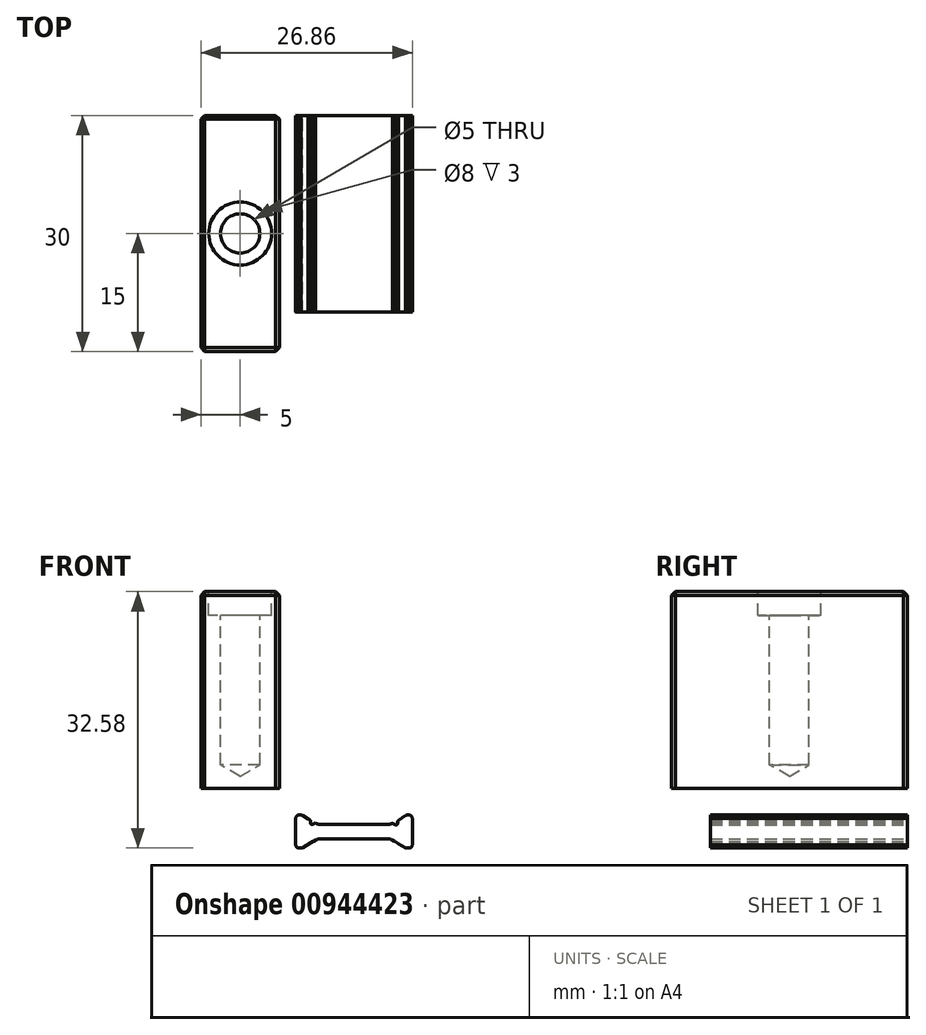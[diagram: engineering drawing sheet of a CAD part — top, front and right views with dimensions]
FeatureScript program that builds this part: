
annotation { "Feature Type Name" : "Feature", "Feature Type Description" : "" }
export const myFeature = defineFeature(function(context is Context, id is Id, definition is map)
    precondition{}
    {
        {
            var Q0;
            Q0=qCreatedBy(makeId("Front.planeOp"),FACE);
            var sketch = newSketch(context, id + "F0", { "sketchPlane" : qUnion([Q0])});
            skArc(sketch, "E0", {"start": v(-30.4, -3.2) * mm, "mid": v(-30.25, -3.55) * mm, "end": v(-29.9, -3.7) * mm});
            skLineSegment(sketch, "E1", {"start": v(-29.9, -3.7) * mm, "end": v(-29.4, -3.7) * mm});
            skArc(sketch, "E2", {"start": v(-29.4, -3.7) * mm, "mid": v(-29.19, -3.61) * mm, "end": v(-29.1, -3.4) * mm});
            skLineSegment(sketch, "E3", {"start": v(-29.1, -3.4) * mm, "end": v(-29.1, -1.7) * mm});
            skLineSegment(sketch, "E4", {"start": v(-29.1, -1.7) * mm, "end": v(-4.3, -1.7) * mm});
            skLineSegment(sketch, "E5", {"start": v(-4.3, -1.7) * mm, "end": v(-4.3, -16.5) * mm});
            skLineSegment(sketch, "E6", {"start": v(-4.3, -16.5) * mm, "end": v(-38.5, -16.5) * mm});
            skLineSegment(sketch, "E7", {"start": v(-38.5, -16.5) * mm, "end": v(-38.5, -7.78) * mm});
            skArc(sketch, "E8", {"start": v(-38.5, -7.78) * mm, "mid": v(-38.1, -6.14) * mm, "end": v(-36.97, -4.89) * mm});
            skArc(sketch, "E9", {"start": v(-36.97, -4.89) * mm, "mid": v(-33.82, -3.17) * mm, "end": v(-30.4, -2.1) * mm});
            skLineSegment(sketch, "E10", {"start": v(-30.4, -2.1) * mm, "end": v(-30.4, -3.2) * mm});
            skArc(sketch, "E11", {"start": v(-2.7, -12.19) * mm, "mid": v(-2.62, -12) * mm, "end": v(-2.43, -11.92) * mm});
            skLineSegment(sketch, "E12", {"start": v(-2.43, -11.92) * mm, "end": v(-2.15, -11.92) * mm});
            skArc(sketch, "E13", {"start": v(-2.15, -11.92) * mm, "mid": v(-2.1, -11.93) * mm, "end": v(-2.05, -11.95) * mm});
            skLineSegment(sketch, "E14", {"start": v(-2.05, -11.95) * mm, "end": v(-0.5, -12.89) * mm});
            skArc(sketch, "E15", {"start": v(-0.5, -12.89) * mm, "mid": v(-0.3, -12.9) * mm, "end": v(-0.2, -12.72) * mm});
            skLineSegment(sketch, "E16", {"start": v(-0.2, -12.72) * mm, "end": v(-0.2, -11.3) * mm});
            skArc(sketch, "E17", {"start": v(-0.2, -11.3) * mm, "mid": v(-0.33, -10.8) * mm, "end": v(-0.68, -10.44) * mm});
            skLineSegment(sketch, "E18", {"start": v(-0.68, -10.44) * mm, "end": v(-2.5, -9.33) * mm});
            skArc(sketch, "E19", {"start": v(-2.5, -9.33) * mm, "mid": v(-2.57, -9.26) * mm, "end": v(-2.6, -9.16) * mm});
            skArc(sketch, "E20", {"start": v(-2.6, -9.16) * mm, "mid": v(-2.57, -9.06) * mm, "end": v(-2.5, -8.99) * mm});
            skLineSegment(sketch, "E21", {"start": v(-2.5, -8.99) * mm, "end": v(-0.68, -7.87) * mm});
            skArc(sketch, "E22", {"start": v(-0.68, -7.87) * mm, "mid": v(-0.33, -7.5) * mm, "end": v(-0.2, -7.02) * mm});
            skLineSegment(sketch, "E23", {"start": v(-0.2, -7.02) * mm, "end": v(-0.2, -5.6) * mm});
            skArc(sketch, "E24", {"start": v(-0.2, -5.6) * mm, "mid": v(-0.3, -5.42) * mm, "end": v(-0.5, -5.43) * mm});
            skLineSegment(sketch, "E25", {"start": v(-0.5, -5.43) * mm, "end": v(-2.05, -6.37) * mm});
            skArc(sketch, "E26", {"start": v(-2.05, -6.37) * mm, "mid": v(-2.1, -6.4) * mm, "end": v(-2.15, -6.4) * mm});
            skLineSegment(sketch, "E27", {"start": v(-2.15, -6.4) * mm, "end": v(-2.43, -6.4) * mm});
            skArc(sketch, "E28", {"start": v(-2.43, -6.4) * mm, "mid": v(-2.62, -6.32) * mm, "end": v(-2.7, -6.13) * mm});
            skLineSegment(sketch, "E29", {"start": v(-2.7, -6.13) * mm, "end": v(-2.7, -2.05) * mm});
            skArc(sketch, "E30", {"start": v(-2.7, -2.05) * mm, "mid": v(-2.7, -2.03) * mm, "end": v(-2.69, -2.01) * mm});
            skArc(sketch, "E31", {"start": v(-2.69, -2.01) * mm, "mid": v(-2.51, -1.78) * mm, "end": v(-2.22, -1.8) * mm});
            skLineSegment(sketch, "E32", {"start": v(-2.22, -1.8) * mm, "end": v(-0.9, -2.7) * mm});
            skArc(sketch, "E33", {"start": v(-0.9, -2.7) * mm, "mid": v(-0.84, -2.78) * mm, "end": v(-0.82, -2.88) * mm});
            skLineSegment(sketch, "E34", {"start": v(-0.82, -2.88) * mm, "end": v(-0.83, -3.05) * mm});
            skArc(sketch, "E35", {"start": v(-0.83, -3.05) * mm, "mid": v(-0.75, -3.23) * mm, "end": v(-0.55, -3.25) * mm});
            skLineSegment(sketch, "E36", {"start": v(-0.55, -3.25) * mm, "end": v(-0.1, -3.03) * mm});
            skArc(sketch, "E37", {"start": v(-0.1, -3.03) * mm, "mid": v(-0.05, -3) * mm, "end": v(-0.01, -2.96) * mm});
            skLineSegment(sketch, "E38", {"start": v(-0.01, -2.96) * mm, "end": v(1.44, -0.66) * mm});
            skArc(sketch, "E39", {"start": v(1.44, -0.66) * mm, "mid": v(1.44, -0.36) * mm, "end": v(1.18, -0.2) * mm});
            skLineSegment(sketch, "E40", {"start": v(1.18, -0.2) * mm, "end": v(-2.75, -0.2) * mm});
            skLineSegment(sketch, "E41", {"start": v(-2.75, -0.2) * mm, "end": v(-16, -0.2) * mm});
            skArc(sketch, "E42", {"start": v(-16, -0.2) * mm, "mid": v(-16.36, -0.05) * mm, "end": v(-16.5, 0.3) * mm});
            skLineSegment(sketch, "E43", {"start": v(-16.5, 0.3) * mm, "end": v(-16.5, 21.41) * mm});
            skArc(sketch, "E44", {"start": v(-16.5, 21.41) * mm, "mid": v(-16.4, 21.64) * mm, "end": v(-16.17, 21.71) * mm});
            skLineSegment(sketch, "E45", {"start": v(-16.17, 21.71) * mm, "end": v(-15.26, 21.6) * mm});
            skArc(sketch, "E46", {"start": v(-15.26, 21.6) * mm, "mid": v(-15.05, 21.69) * mm, "end": v(-14.96, 21.9) * mm});
            skLineSegment(sketch, "E47", {"start": v(-14.96, 21.9) * mm, "end": v(-14.96, 23.3) * mm});
            skArc(sketch, "E48", {"start": v(-14.96, 23.3) * mm, "mid": v(-15.02, 23.48) * mm, "end": v(-15.18, 23.58) * mm});
            skLineSegment(sketch, "E49", {"start": v(-15.18, 23.58) * mm, "end": v(-22.2, 25.46) * mm});
            skArc(sketch, "E50", {"start": v(-22.2, 25.46) * mm, "mid": v(-22.46, 25.5) * mm, "end": v(-22.72, 25.46) * mm});
            skLineSegment(sketch, "E51", {"start": v(-22.72, 25.46) * mm, "end": v(-29.73, 23.58) * mm});
            skArc(sketch, "E52", {"start": v(-29.73, 23.58) * mm, "mid": v(-29.9, 23.48) * mm, "end": v(-29.96, 23.3) * mm});
            skLineSegment(sketch, "E53", {"start": v(-29.96, 23.3) * mm, "end": v(-29.96, 14.56) * mm});
            skArc(sketch, "E54", {"start": v(-29.96, 14.56) * mm, "mid": v(-29.49, 13.28) * mm, "end": v(-28.3, 12.6) * mm});
            skLineSegment(sketch, "E55", {"start": v(-28.3, 12.6) * mm, "end": v(-27.31, 12.42) * mm});
            skArc(sketch, "E56", {"start": v(-27.31, 12.42) * mm, "mid": v(-27.07, 12.48) * mm, "end": v(-26.96, 12.71) * mm});
            skLineSegment(sketch, "E57", {"start": v(-26.96, 12.71) * mm, "end": v(-26.96, 13.52) * mm});
            skArc(sketch, "E58", {"start": v(-26.96, 13.52) * mm, "mid": v(-27.03, 13.72) * mm, "end": v(-27.2, 13.82) * mm});
            skLineSegment(sketch, "E59", {"start": v(-27.2, 13.82) * mm, "end": v(-28.3, 14.01) * mm});
            skArc(sketch, "E60", {"start": v(-28.3, 14.01) * mm, "mid": v(-28.49, 14.12) * mm, "end": v(-28.56, 14.3) * mm});
            skLineSegment(sketch, "E61", {"start": v(-28.56, 14.3) * mm, "end": v(-28.56, 22.01) * mm});
            skArc(sketch, "E62", {"start": v(-28.56, 22.01) * mm, "mid": v(-28.5, 22.2) * mm, "end": v(-28.33, 22.3) * mm});
            skLineSegment(sketch, "E63", {"start": v(-28.33, 22.3) * mm, "end": v(-24.76, 23.26) * mm});
            skArc(sketch, "E64", {"start": v(-24.76, 23.26) * mm, "mid": v(-24.7, 23.27) * mm, "end": v(-24.64, 23.28) * mm});
            skArc(sketch, "E65", {"start": v(-24.64, 23.28) * mm, "mid": v(-22.46, 23.3) * mm, "end": v(-20.27, 23.28) * mm});
            skArc(sketch, "E66", {"start": v(-20.27, 23.28) * mm, "mid": v(-20.21, 23.27) * mm, "end": v(-20.15, 23.26) * mm});
            skLineSegment(sketch, "E67", {"start": v(-20.15, 23.26) * mm, "end": v(-18.33, 22.77) * mm});
            skArc(sketch, "E68", {"start": v(-18.33, 22.77) * mm, "mid": v(-18.17, 22.66) * mm, "end": v(-18.1, 22.48) * mm});
            skLineSegment(sketch, "E69", {"start": v(-18.1, 22.48) * mm, "end": v(-18.1, 1.4) * mm});
            skArc(sketch, "E70", {"start": v(-18.1, 1.4) * mm, "mid": v(-18.2, 1.19) * mm, "end": v(-18.4, 1.1) * mm});
            skLineSegment(sketch, "E71", {"start": v(-18.4, 1.1) * mm, "end": v(-18.8, 1.1) * mm});
            skArc(sketch, "E72", {"start": v(-18.8, 1.1) * mm, "mid": v(-19.02, 1.01) * mm, "end": v(-19.1, 0.8) * mm});
            skArc(sketch, "E73", {"start": v(-19.1, 0.8) * mm, "mid": v(-19.4, 0.1) * mm, "end": v(-20.1, -0.2) * mm});
            skLineSegment(sketch, "E74", {"start": v(-20.1, -0.2) * mm, "end": v(-26.58, -0.2) * mm});
            skArc(sketch, "E75", {"start": v(-26.58, -0.2) * mm, "mid": v(-32.45, -1.08) * mm, "end": v(-37.8, -3.64) * mm});
            skArc(sketch, "E76", {"start": v(-37.8, -3.64) * mm, "mid": v(-39.42, -5.44) * mm, "end": v(-40, -7.78) * mm});
            skLineSegment(sketch, "E77", {"start": v(-40, -7.78) * mm, "end": v(-40, -25.2) * mm});
            skArc(sketch, "E78", {"start": v(-40, -25.2) * mm, "mid": v(-39.91, -25.41) * mm, "end": v(-39.7, -25.5) * mm});
            skLineSegment(sketch, "E79", {"start": v(-39.7, -25.5) * mm, "end": v(-37.42, -25.5) * mm});
            skArc(sketch, "E80", {"start": v(-37.42, -25.5) * mm, "mid": v(-37.17, -25.43) * mm, "end": v(-37, -25.25) * mm});
            skLineSegment(sketch, "E81", {"start": v(-37, -25.25) * mm, "end": v(-36.82, -24.95) * mm});
            skArc(sketch, "E82", {"start": v(-36.82, -24.95) * mm, "mid": v(-36.82, -24.45) * mm, "end": v(-37.25, -24.2) * mm});
            skLineSegment(sketch, "E83", {"start": v(-37.25, -24.2) * mm, "end": v(-38.6, -24.2) * mm});
            skLineSegment(sketch, "E84", {"start": v(-38.6, -24.2) * mm, "end": v(-38.6, -18) * mm});
            skLineSegment(sketch, "E85", {"start": v(-38.6, -18) * mm, "end": v(-4.5, -18) * mm});
            skArc(sketch, "E86", {"start": v(-4.5, -18) * mm, "mid": v(-4.29, -18.09) * mm, "end": v(-4.2, -18.3) * mm});
            skLineSegment(sketch, "E87", {"start": v(-4.2, -18.3) * mm, "end": v(-4.2, -24.1) * mm});
            skLineSegment(sketch, "E88", {"start": v(-4.2, -24.1) * mm, "end": v(-10.4, -24.1) * mm});
            skArc(sketch, "E89", {"start": v(-10.4, -24.1) * mm, "mid": v(-10.75, -24.24) * mm, "end": v(-10.9, -24.6) * mm});
            skLineSegment(sketch, "E90", {"start": v(-10.9, -24.6) * mm, "end": v(-10.9, -24.9) * mm});
            skArc(sketch, "E91", {"start": v(-10.9, -24.9) * mm, "mid": v(-10.75, -25.25) * mm, "end": v(-10.4, -25.4) * mm});
            skLineSegment(sketch, "E92", {"start": v(-10.4, -25.4) * mm, "end": v(-7.85, -25.4) * mm});
            skLineSegment(sketch, "E93", {"start": v(-7.85, -25.4) * mm, "end": v(-7.55, -25.1) * mm});
            skLineSegment(sketch, "E94", {"start": v(-7.55, -25.1) * mm, "end": v(-7.25, -25.4) * mm});
            skLineSegment(sketch, "E95", {"start": v(-7.25, -25.4) * mm, "end": v(-3.2, -25.4) * mm});
            skArc(sketch, "E96", {"start": v(-3.2, -25.4) * mm, "mid": v(-2.99, -25.31) * mm, "end": v(-2.9, -25.1) * mm});
            skLineSegment(sketch, "E97", {"start": v(-2.9, -25.1) * mm, "end": v(-2.9, -18.3) * mm});
            skArc(sketch, "E98", {"start": v(-2.9, -18.3) * mm, "mid": v(-2.81, -18.09) * mm, "end": v(-2.6, -18) * mm});
            skLineSegment(sketch, "E99", {"start": v(-2.6, -18) * mm, "end": v(1.17, -18) * mm});
            skArc(sketch, "E100", {"start": v(1.17, -18) * mm, "mid": v(1.44, -17.84) * mm, "end": v(1.43, -17.54) * mm});
            skLineSegment(sketch, "E101", {"start": v(1.43, -17.54) * mm, "end": v(-0.02, -15.24) * mm});
            skArc(sketch, "E102", {"start": v(-0.02, -15.24) * mm, "mid": v(-0.06, -15.2) * mm, "end": v(-0.1, -15.17) * mm});
            skLineSegment(sketch, "E103", {"start": v(-0.1, -15.17) * mm, "end": v(-0.55, -14.95) * mm});
            skArc(sketch, "E104", {"start": v(-0.55, -14.95) * mm, "mid": v(-0.75, -14.96) * mm, "end": v(-0.84, -15.14) * mm});
            skLineSegment(sketch, "E105", {"start": v(-0.84, -15.14) * mm, "end": v(-0.83, -15.32) * mm});
            skArc(sketch, "E106", {"start": v(-0.83, -15.32) * mm, "mid": v(-0.85, -15.42) * mm, "end": v(-0.91, -15.5) * mm});
            skLineSegment(sketch, "E107", {"start": v(-0.91, -15.5) * mm, "end": v(-2.23, -16.4) * mm});
            skArc(sketch, "E108", {"start": v(-2.23, -16.4) * mm, "mid": v(-2.54, -16.4) * mm, "end": v(-2.7, -16.14) * mm});
            skLineSegment(sketch, "E109", {"start": v(-2.7, -16.14) * mm, "end": v(-2.7, -12.19) * mm});
            skLineSegment(sketch, "E110", {"start": v(8.94, -5.07) * mm, "end": v(0.46, -5.07) * mm});
            skArc(sketch, "E111", {"start": v(0.46, -5.07) * mm, "mid": v(0.15, -5.11) * mm, "end": v(-0.14, -5.23) * mm});
            skLineSegment(sketch, "E112", {"start": v(-0.14, -5.23) * mm, "end": v(-1.85, -6.22) * mm});
            skArc(sketch, "E113", {"start": v(-1.85, -6.22) * mm, "mid": v(-1.94, -6.26) * mm, "end": v(-2.05, -6.27) * mm});
            skLineSegment(sketch, "E114", {"start": v(-2.05, -6.27) * mm, "end": v(-2.3, -6.27) * mm});
            skArc(sketch, "E115", {"start": v(-2.3, -6.27) * mm, "mid": v(-2.58, -6.15) * mm, "end": v(-2.7, -5.87) * mm});
            skLineSegment(sketch, "E116", {"start": v(-2.7, -5.87) * mm, "end": v(-2.7, -2.47) * mm});
            skArc(sketch, "E117", {"start": v(-2.7, -2.47) * mm, "mid": v(-2.58, -2.19) * mm, "end": v(-2.3, -2.07) * mm});
            skLineSegment(sketch, "E118", {"start": v(-2.3, -2.07) * mm, "end": v(-2.05, -2.07) * mm});
            skArc(sketch, "E119", {"start": v(-2.05, -2.07) * mm, "mid": v(-1.94, -2.09) * mm, "end": v(-1.85, -2.13) * mm});
            skLineSegment(sketch, "E120", {"start": v(-1.85, -2.13) * mm, "end": v(-0.14, -3.11) * mm});
            skArc(sketch, "E121", {"start": v(-0.14, -3.11) * mm, "mid": v(0.15, -3.23) * mm, "end": v(0.46, -3.27) * mm});
            skLineSegment(sketch, "E122", {"start": v(0.46, -3.27) * mm, "end": v(8.94, -3.27) * mm});
            skArc(sketch, "E123", {"start": v(8.94, -3.27) * mm, "mid": v(9.25, -3.23) * mm, "end": v(9.54, -3.11) * mm});
            skLineSegment(sketch, "E124", {"start": v(9.54, -3.11) * mm, "end": v(11.25, -2.13) * mm});
            skArc(sketch, "E125", {"start": v(11.25, -2.13) * mm, "mid": v(11.34, -2.09) * mm, "end": v(11.45, -2.07) * mm});
            skLineSegment(sketch, "E126", {"start": v(11.45, -2.07) * mm, "end": v(11.7, -2.07) * mm});
            skArc(sketch, "E127", {"start": v(11.7, -2.07) * mm, "mid": v(11.98, -2.19) * mm, "end": v(12.1, -2.47) * mm});
            skLineSegment(sketch, "E128", {"start": v(12.1, -2.47) * mm, "end": v(12.1, -5.87) * mm});
            skArc(sketch, "E129", {"start": v(12.1, -5.87) * mm, "mid": v(11.98, -6.15) * mm, "end": v(11.7, -6.27) * mm});
            skLineSegment(sketch, "E130", {"start": v(11.7, -6.27) * mm, "end": v(11.45, -6.27) * mm});
            skArc(sketch, "E131", {"start": v(11.45, -6.27) * mm, "mid": v(11.34, -6.26) * mm, "end": v(11.25, -6.22) * mm});
            skLineSegment(sketch, "E132", {"start": v(11.25, -6.22) * mm, "end": v(9.54, -5.23) * mm});
            skArc(sketch, "E133", {"start": v(9.54, -5.23) * mm, "mid": v(9.25, -5.11) * mm, "end": v(8.94, -5.07) * mm});
            skLineSegment(sketch, "E134", {"start": v(8.94, -13.24) * mm, "end": v(0.46, -13.24) * mm});
            skArc(sketch, "E135", {"start": v(0.46, -13.24) * mm, "mid": v(0.15, -13.2) * mm, "end": v(-0.14, -13.07) * mm});
            skLineSegment(sketch, "E136", {"start": v(-0.14, -13.07) * mm, "end": v(-1.85, -12.09) * mm});
            skArc(sketch, "E137", {"start": v(-1.85, -12.09) * mm, "mid": v(-1.94, -12.05) * mm, "end": v(-2.05, -12.04) * mm});
            skLineSegment(sketch, "E138", {"start": v(-2.05, -12.04) * mm, "end": v(-2.3, -12.04) * mm});
            skArc(sketch, "E139", {"start": v(-2.3, -12.04) * mm, "mid": v(-2.58, -12.15) * mm, "end": v(-2.7, -12.44) * mm});
            skLineSegment(sketch, "E140", {"start": v(-2.7, -12.44) * mm, "end": v(-2.7, -15.84) * mm});
            skArc(sketch, "E141", {"start": v(-2.7, -15.84) * mm, "mid": v(-2.58, -16.12) * mm, "end": v(-2.3, -16.24) * mm});
            skLineSegment(sketch, "E142", {"start": v(-2.3, -16.24) * mm, "end": v(-2.05, -16.24) * mm});
            skArc(sketch, "E143", {"start": v(-2.05, -16.24) * mm, "mid": v(-1.94, -16.22) * mm, "end": v(-1.85, -16.18) * mm});
            skLineSegment(sketch, "E144", {"start": v(-1.85, -16.18) * mm, "end": v(-0.14, -15.2) * mm});
            skArc(sketch, "E145", {"start": v(-0.14, -15.2) * mm, "mid": v(0.15, -15.08) * mm, "end": v(0.46, -15.04) * mm});
            skLineSegment(sketch, "E146", {"start": v(0.46, -15.04) * mm, "end": v(8.94, -15.04) * mm});
            skArc(sketch, "E147", {"start": v(8.94, -15.04) * mm, "mid": v(9.25, -15.08) * mm, "end": v(9.54, -15.2) * mm});
            skLineSegment(sketch, "E148", {"start": v(9.54, -15.2) * mm, "end": v(11.25, -16.18) * mm});
            skArc(sketch, "E149", {"start": v(11.25, -16.18) * mm, "mid": v(11.34, -16.22) * mm, "end": v(11.45, -16.24) * mm});
            skLineSegment(sketch, "E150", {"start": v(11.45, -16.24) * mm, "end": v(11.7, -16.24) * mm});
            skArc(sketch, "E151", {"start": v(11.7, -16.24) * mm, "mid": v(11.98, -16.12) * mm, "end": v(12.1, -15.84) * mm});
            skLineSegment(sketch, "E152", {"start": v(12.1, -15.84) * mm, "end": v(12.1, -12.44) * mm});
            skArc(sketch, "E153", {"start": v(12.1, -12.44) * mm, "mid": v(11.98, -12.15) * mm, "end": v(11.7, -12.04) * mm});
            skLineSegment(sketch, "E154", {"start": v(11.7, -12.04) * mm, "end": v(11.45, -12.04) * mm});
            skArc(sketch, "E155", {"start": v(11.45, -12.04) * mm, "mid": v(11.34, -12.05) * mm, "end": v(11.25, -12.09) * mm});
            skLineSegment(sketch, "E156", {"start": v(11.25, -12.09) * mm, "end": v(9.54, -13.07) * mm});
            skArc(sketch, "E157", {"start": v(9.54, -13.07) * mm, "mid": v(9.25, -13.2) * mm, "end": v(8.94, -13.24) * mm});
            skLineSegment(sketch, "E158", {"start": v(13.7, -16.5) * mm, "end": v(13.7, -1.3) * mm});
            skLineSegment(sketch, "E159", {"start": v(13.7, -1.3) * mm, "end": v(16.4, -1.3) * mm});
            skArc(sketch, "E160", {"start": v(16.4, -1.3) * mm, "mid": v(16.61, -1.2) * mm, "end": v(16.7, -1) * mm});
            skLineSegment(sketch, "E161", {"start": v(16.7, -1) * mm, "end": v(16.7, -0.35) * mm});
            skArc(sketch, "E162", {"start": v(16.7, -0.35) * mm, "mid": v(16.78, -0.14) * mm, "end": v(16.99, -0.05) * mm});
            skArc(sketch, "E163", {"start": v(16.99, -0.05) * mm, "mid": v(27.75, 1.43) * mm, "end": v(38.08, 4.8) * mm});
            skArc(sketch, "E164", {"start": v(38.08, 4.8) * mm, "mid": v(38.37, 4.76) * mm, "end": v(38.5, 4.51) * mm});
            skLineSegment(sketch, "E165", {"start": v(38.5, 4.51) * mm, "end": v(38.5, 0.5) * mm});
            skLineSegment(sketch, "E166", {"start": v(38.5, 0.5) * mm, "end": v(35.47, -0.37) * mm});
            skArc(sketch, "E167", {"start": v(35.47, -0.37) * mm, "mid": v(35.31, -0.47) * mm, "end": v(35.25, -0.66) * mm});
            skLineSegment(sketch, "E168", {"start": v(35.25, -0.66) * mm, "end": v(35.25, -1) * mm});
            skArc(sketch, "E169", {"start": v(35.25, -1) * mm, "mid": v(35.34, -1.2) * mm, "end": v(35.55, -1.3) * mm});
            skLineSegment(sketch, "E170", {"start": v(35.55, -1.3) * mm, "end": v(38.5, -1.3) * mm});
            skLineSegment(sketch, "E171", {"start": v(38.5, -1.3) * mm, "end": v(38.5, -16.5) * mm});
            skLineSegment(sketch, "E172", {"start": v(38.5, -16.5) * mm, "end": v(13.7, -16.5) * mm});
            skArc(sketch, "E173", {"start": v(14, 1.38) * mm, "mid": v(13.78, 1.46) * mm, "end": v(13.7, 1.68) * mm});
            skLineSegment(sketch, "E174", {"start": v(13.7, 1.68) * mm, "end": v(13.7, 22.48) * mm});
            skArc(sketch, "E175", {"start": v(13.7, 22.48) * mm, "mid": v(13.75, 22.66) * mm, "end": v(13.92, 22.77) * mm});
            skLineSegment(sketch, "E176", {"start": v(13.92, 22.77) * mm, "end": v(15.74, 23.26) * mm});
            skArc(sketch, "E177", {"start": v(15.74, 23.26) * mm, "mid": v(15.8, 23.27) * mm, "end": v(15.86, 23.28) * mm});
            skArc(sketch, "E178", {"start": v(15.86, 23.28) * mm, "mid": v(18.04, 23.3) * mm, "end": v(20.23, 23.28) * mm});
            skArc(sketch, "E179", {"start": v(20.23, 23.28) * mm, "mid": v(20.29, 23.27) * mm, "end": v(20.35, 23.26) * mm});
            skLineSegment(sketch, "E180", {"start": v(20.35, 23.26) * mm, "end": v(23.92, 22.3) * mm});
            skArc(sketch, "E181", {"start": v(23.92, 22.3) * mm, "mid": v(24.08, 22.2) * mm, "end": v(24.14, 22.01) * mm});
            skLineSegment(sketch, "E182", {"start": v(24.14, 22.01) * mm, "end": v(24.14, 14.3) * mm});
            skArc(sketch, "E183", {"start": v(24.14, 14.3) * mm, "mid": v(24.07, 14.12) * mm, "end": v(23.9, 14.01) * mm});
            skLineSegment(sketch, "E184", {"start": v(23.9, 14.01) * mm, "end": v(22.8, 13.82) * mm});
            skArc(sketch, "E185", {"start": v(22.8, 13.82) * mm, "mid": v(22.61, 13.72) * mm, "end": v(22.54, 13.52) * mm});
            skLineSegment(sketch, "E186", {"start": v(22.54, 13.52) * mm, "end": v(22.54, 12.71) * mm});
            skArc(sketch, "E187", {"start": v(22.54, 12.71) * mm, "mid": v(22.65, 12.48) * mm, "end": v(22.9, 12.42) * mm});
            skLineSegment(sketch, "E188", {"start": v(22.9, 12.42) * mm, "end": v(23.89, 12.6) * mm});
            skArc(sketch, "E189", {"start": v(23.89, 12.6) * mm, "mid": v(25.07, 13.28) * mm, "end": v(25.54, 14.56) * mm});
            skLineSegment(sketch, "E190", {"start": v(25.54, 14.56) * mm, "end": v(25.54, 23.3) * mm});
            skArc(sketch, "E191", {"start": v(25.54, 23.3) * mm, "mid": v(25.48, 23.48) * mm, "end": v(25.32, 23.58) * mm});
            skLineSegment(sketch, "E192", {"start": v(25.32, 23.58) * mm, "end": v(18.3, 25.46) * mm});
            skArc(sketch, "E193", {"start": v(18.3, 25.46) * mm, "mid": v(18.04, 25.5) * mm, "end": v(17.78, 25.46) * mm});
            skLineSegment(sketch, "E194", {"start": v(17.78, 25.46) * mm, "end": v(10.77, 23.58) * mm});
            skArc(sketch, "E195", {"start": v(10.77, 23.58) * mm, "mid": v(10.6, 23.48) * mm, "end": v(10.54, 23.3) * mm});
            skLineSegment(sketch, "E196", {"start": v(10.54, 23.3) * mm, "end": v(10.54, 21.9) * mm});
            skArc(sketch, "E197", {"start": v(10.54, 21.9) * mm, "mid": v(10.63, 21.69) * mm, "end": v(10.84, 21.6) * mm});
            skLineSegment(sketch, "E198", {"start": v(10.84, 21.6) * mm, "end": v(11.76, 21.71) * mm});
            skArc(sketch, "E199", {"start": v(11.76, 21.71) * mm, "mid": v(12, 21.64) * mm, "end": v(12.1, 21.41) * mm});
            skLineSegment(sketch, "E200", {"start": v(12.1, 21.41) * mm, "end": v(12.1, 0.05) * mm});
            skArc(sketch, "E201", {"start": v(12.1, 0.05) * mm, "mid": v(12, -0.16) * mm, "end": v(11.8, -0.25) * mm});
            skLineSegment(sketch, "E202", {"start": v(11.8, -0.25) * mm, "end": v(8.25, -0.25) * mm});
            skArc(sketch, "E203", {"start": v(8.25, -0.25) * mm, "mid": v(7.99, -0.4) * mm, "end": v(8, -0.7) * mm});
            skLineSegment(sketch, "E204", {"start": v(8, -0.7) * mm, "end": v(9.44, -3) * mm});
            skArc(sketch, "E205", {"start": v(9.44, -3) * mm, "mid": v(9.48, -3.05) * mm, "end": v(9.52, -3.08) * mm});
            skLineSegment(sketch, "E206", {"start": v(9.52, -3.08) * mm, "end": v(9.98, -3.3) * mm});
            skArc(sketch, "E207", {"start": v(9.98, -3.3) * mm, "mid": v(10.18, -3.28) * mm, "end": v(10.26, -3.1) * mm});
            skLineSegment(sketch, "E208", {"start": v(10.26, -3.1) * mm, "end": v(10.25, -2.93) * mm});
            skArc(sketch, "E209", {"start": v(10.25, -2.93) * mm, "mid": v(10.27, -2.83) * mm, "end": v(10.34, -2.75) * mm});
            skLineSegment(sketch, "E210", {"start": v(10.34, -2.75) * mm, "end": v(11.63, -1.87) * mm});
            skArc(sketch, "E211", {"start": v(11.63, -1.87) * mm, "mid": v(11.94, -1.85) * mm, "end": v(12.1, -2.12) * mm});
            skLineSegment(sketch, "E212", {"start": v(12.1, -2.12) * mm, "end": v(12.1, -6.13) * mm});
            skArc(sketch, "E213", {"start": v(12.1, -6.13) * mm, "mid": v(12.02, -6.32) * mm, "end": v(11.83, -6.4) * mm});
            skLineSegment(sketch, "E214", {"start": v(11.83, -6.4) * mm, "end": v(11.56, -6.4) * mm});
            skArc(sketch, "E215", {"start": v(11.56, -6.4) * mm, "mid": v(11.5, -6.4) * mm, "end": v(11.45, -6.37) * mm});
            skLineSegment(sketch, "E216", {"start": v(11.45, -6.37) * mm, "end": v(9.91, -5.43) * mm});
            skArc(sketch, "E217", {"start": v(9.91, -5.43) * mm, "mid": v(9.7, -5.42) * mm, "end": v(9.6, -5.6) * mm});
            skLineSegment(sketch, "E218", {"start": v(9.6, -5.6) * mm, "end": v(9.6, -7.02) * mm});
            skArc(sketch, "E219", {"start": v(9.6, -7.02) * mm, "mid": v(9.73, -7.5) * mm, "end": v(10.08, -7.87) * mm});
            skLineSegment(sketch, "E220", {"start": v(10.08, -7.87) * mm, "end": v(11.9, -8.99) * mm});
            skArc(sketch, "E221", {"start": v(11.9, -8.99) * mm, "mid": v(11.98, -9.06) * mm, "end": v(12, -9.16) * mm});
            skArc(sketch, "E222", {"start": v(12, -9.16) * mm, "mid": v(11.98, -9.26) * mm, "end": v(11.9, -9.33) * mm});
            skLineSegment(sketch, "E223", {"start": v(11.9, -9.33) * mm, "end": v(10.08, -10.44) * mm});
            skArc(sketch, "E224", {"start": v(10.08, -10.44) * mm, "mid": v(9.73, -10.8) * mm, "end": v(9.6, -11.3) * mm});
            skLineSegment(sketch, "E225", {"start": v(9.6, -11.3) * mm, "end": v(9.6, -12.72) * mm});
            skArc(sketch, "E226", {"start": v(9.6, -12.72) * mm, "mid": v(9.7, -12.9) * mm, "end": v(9.91, -12.89) * mm});
            skLineSegment(sketch, "E227", {"start": v(9.91, -12.89) * mm, "end": v(11.45, -11.95) * mm});
            skArc(sketch, "E228", {"start": v(11.45, -11.95) * mm, "mid": v(11.5, -11.93) * mm, "end": v(11.56, -11.92) * mm});
            skLineSegment(sketch, "E229", {"start": v(11.56, -11.92) * mm, "end": v(11.83, -11.92) * mm});
            skArc(sketch, "E230", {"start": v(11.83, -11.92) * mm, "mid": v(12.02, -12) * mm, "end": v(12.1, -12.19) * mm});
            skLineSegment(sketch, "E231", {"start": v(12.1, -12.19) * mm, "end": v(12.1, -16.16) * mm});
            skArc(sketch, "E232", {"start": v(12.1, -16.16) * mm, "mid": v(11.94, -16.43) * mm, "end": v(11.63, -16.4) * mm});
            skLineSegment(sketch, "E233", {"start": v(11.63, -16.4) * mm, "end": v(10.29, -15.5) * mm});
            skArc(sketch, "E234", {"start": v(10.29, -15.5) * mm, "mid": v(10.22, -15.42) * mm, "end": v(10.2, -15.32) * mm});
            skLineSegment(sketch, "E235", {"start": v(10.2, -15.32) * mm, "end": v(10.21, -15.14) * mm});
            skArc(sketch, "E236", {"start": v(10.21, -15.14) * mm, "mid": v(10.13, -14.96) * mm, "end": v(9.93, -14.95) * mm});
            skLineSegment(sketch, "E237", {"start": v(9.93, -14.95) * mm, "end": v(9.48, -15.17) * mm});
            skArc(sketch, "E238", {"start": v(9.48, -15.17) * mm, "mid": v(9.43, -15.2) * mm, "end": v(9.4, -15.24) * mm});
            skLineSegment(sketch, "E239", {"start": v(9.4, -15.24) * mm, "end": v(7.95, -17.54) * mm});
            skArc(sketch, "E240", {"start": v(7.95, -17.54) * mm, "mid": v(7.94, -17.84) * mm, "end": v(8.2, -18) * mm});
            skLineSegment(sketch, "E241", {"start": v(8.2, -18) * mm, "end": v(12.53, -18) * mm});
            skLineSegment(sketch, "E242", {"start": v(12.53, -18) * mm, "end": v(13.7, -18) * mm});
            skLineSegment(sketch, "E243", {"start": v(13.7, -18) * mm, "end": v(13.7, -25) * mm});
            skArc(sketch, "E244", {"start": v(13.7, -25) * mm, "mid": v(13.79, -25.21) * mm, "end": v(14, -25.3) * mm});
            skLineSegment(sketch, "E245", {"start": v(14, -25.3) * mm, "end": v(14.7, -25.3) * mm});
            skArc(sketch, "E246", {"start": v(14.7, -25.3) * mm, "mid": v(14.91, -25.21) * mm, "end": v(15, -25) * mm});
            skLineSegment(sketch, "E247", {"start": v(15, -25) * mm, "end": v(15, -18) * mm});
            skLineSegment(sketch, "E248", {"start": v(15, -18) * mm, "end": v(38.6, -18) * mm});
            skLineSegment(sketch, "E249", {"start": v(38.6, -18) * mm, "end": v(38.6, -24.2) * mm});
            skLineSegment(sketch, "E250", {"start": v(38.6, -24.2) * mm, "end": v(37.25, -24.2) * mm});
            skArc(sketch, "E251", {"start": v(37.25, -24.2) * mm, "mid": v(36.82, -24.45) * mm, "end": v(36.82, -24.95) * mm});
            skLineSegment(sketch, "E252", {"start": v(36.82, -24.95) * mm, "end": v(37, -25.25) * mm});
            skArc(sketch, "E253", {"start": v(37, -25.25) * mm, "mid": v(37.17, -25.43) * mm, "end": v(37.42, -25.5) * mm});
            skLineSegment(sketch, "E254", {"start": v(37.42, -25.5) * mm, "end": v(39.7, -25.5) * mm});
            skArc(sketch, "E255", {"start": v(39.7, -25.5) * mm, "mid": v(39.91, -25.41) * mm, "end": v(40, -25.2) * mm});
            skLineSegment(sketch, "E256", {"start": v(40, -25.2) * mm, "end": v(40, 18.75) * mm});
            skArc(sketch, "E257", {"start": v(40, 18.75) * mm, "mid": v(39.25, 19.5) * mm, "end": v(38.5, 18.75) * mm});
            skLineSegment(sketch, "E258", {"start": v(38.5, 18.75) * mm, "end": v(38.45, 9.9) * mm});
            skArc(sketch, "E259", {"start": v(38.45, 9.9) * mm, "mid": v(37.55, 7.08) * mm, "end": v(35.22, 5.26) * mm});
            skArc(sketch, "E260", {"start": v(35.22, 5.26) * mm, "mid": v(24.78, 2.35) * mm, "end": v(14, 1.38) * mm});
            skLineSegment(sketch, "E261.bottom", {"start": v(-14.76, 26.31) * mm, "end": v(-4.76, 26.31) * mm});
            skLineSegment(sketch, "E261.top", {"start": v(-14.76, 1.31) * mm, "end": v(-4.76, 1.31) * mm});
            skLineSegment(sketch, "E261.left", {"start": v(-14.76, 26.31) * mm, "end": v(-14.76, 1.31) * mm});
            skLineSegment(sketch, "E261.right", {"start": v(-4.76, 26.31) * mm, "end": v(-4.76, 1.31) * mm});
            skSolve(sketch);
        }
        {
            var Q0;
            Q0=makeQuery(id+"F0.imprint","IMPRINT",FACE,{"disambiguationData":[TD([[makeQuery(id+"F0.imprint","IMPRINT",EDGE,{"derivedFrom":sQuery(id+"F0.wireOp",EDGE,"E261.bottom")}),-1.0]])]});
            extrude(context, id + "F1", {"entities" : qUnion([Q0]), "depth" : 30 * mm, "offsetDistance" : 25 * mm});
        }
        {
            var Q0;
            Q0=makeQuery(id+"F1.opExtrude","SWEPT_FACE",FACE,{"disambiguationData":[OSD([sQuery(id+"F0.wireOp",EDGE,"E261.bottom")])]});
            var sketch = newSketch(context, id + "F2", { "sketchPlane" : qUnion([Q0])});
            skPoint(sketch, "E262", {"position": v(-9.76, -15) * mm});
            skPoint(sketch, "E262.positionSnap0", {"position": v(-4.76, -15) * mm});
            skPoint(sketch, "E262.positionSnap1", {"position": v(-9.76, -30) * mm});
            skSolve(sketch);
        }
        {
            var Q0;
            Q0=sQuery(id+"F2.wireOp",VERTEX,"E262");
            var Q1;
            Q1=makeQuery(id+"F1.opExtrude","SWEPT_BODY",BODY,{"disambiguationData":[OSD([sQuery(id+"F0.wireOp",EDGE,"E261.bottom"),sQuery(id+"F0.wireOp",EDGE,"E261.top"),sQuery(id+"F0.wireOp",EDGE,"E261.left"),sQuery(id+"F0.wireOp",EDGE,"E261.right")])]});
            hole(context, id + "F3", {"style" : HoleStyle.C_BORE, "endStyle" : HoleEndStyle.BLIND, "holeDiameter" : 5 * mm, "cBoreDiameter" : 8 * mm, "cBoreDepth" : 3 * mm, "majorDiameter" : 5 * mm, "holeDepth" : 22 * mm, "isTappedThrough" : true, "tappedDepth" : 12 * mm, "tapClearance" : 3, "startFromSketch" : true, "locations" : qUnion([Q0]), "scope" : qUnion([Q1])});
        }
        {
            var Q0;
            {var subQ1=sQuery(id+"F0.wireOp",EDGE,"E33");Q0=makeQuery(id+"F0.imprint","IMPRINT",FACE,{"disambiguationData":[TD([[makeQuery(id+"F0.imprint","IMPRINT",EDGE,{"derivedFrom":subQ1}),1.0]])]});}
            var Q1;
            Q1=makeQuery(id+"F0.imprint","IMPRINT",FACE,{"disambiguationData":[TD([[makeQuery(id+"F0.imprint","IMPRINT",EDGE,{"derivedFrom":sQuery(id+"F0.wireOp",EDGE,"E0")}),1.0]])]});
            var Q2;
            {var subQ39=sQuery(id+"F0.wireOp",EDGE,"E148");Q2=makeQuery(id+"F0.imprint","IMPRINT",FACE,{"disambiguationData":[TD([[makeQuery(id+"F0.imprint","IMPRINT",EDGE,{"derivedFrom":subQ39}),-1.0]])]});}
            extrude(context, id + "F4", {"entities" : qUnion([Q0, Q1, Q2]), "operationType" : NewBodyOperationType.ADD, "depth" : 25 * mm, "offsetDistance" : 25 * mm});
        }
        {
            var Q0;
            Q0=makeQuery(id+"F1.opExtrude","CAP_EDGE",EDGE,{"disambiguationData":[OSD([sQuery(id+"F0.wireOp",EDGE,"E261.bottom")])],"isStart":false});
            var Q1;
            Q1=makeQuery(id+"F1.opExtrude","CAP_EDGE",EDGE,{"disambiguationData":[OSD([sQuery(id+"F0.wireOp",EDGE,"E261.left")])],"isStart":false});
            var Q2;
            Q2=makeQuery(id+"F1.opExtrude","CAP_EDGE",EDGE,{"disambiguationData":[OSD([sQuery(id+"F0.wireOp",EDGE,"E261.right")])],"isStart":false});
            var Q3;
            Q3=makeQuery(id+"F1.opExtrude","SWEPT_EDGE",EDGE,{"disambiguationData":[OSD([sQuery(id+"F0.wireOp",EDGE,"E261.bottom"),sQuery(id+"F0.wireOp",EDGE,"E261.left")])]});
            var Q4;
            Q4=makeQuery(id+"F1.opExtrude","SWEPT_EDGE",EDGE,{"disambiguationData":[OSD([sQuery(id+"F0.wireOp",EDGE,"E261.bottom"),sQuery(id+"F0.wireOp",EDGE,"E261.right")])]});
            var Q5;
            Q5=makeQuery(id+"F1.opExtrude","CAP_EDGE",EDGE,{"disambiguationData":[OSD([sQuery(id+"F0.wireOp",EDGE,"E261.bottom")])],"isStart":true});
            var Q6;
            Q6=makeQuery(id+"F1.opExtrude","CAP_EDGE",EDGE,{"disambiguationData":[OSD([sQuery(id+"F0.wireOp",EDGE,"E261.right")])],"isStart":true});
            var Q7;
            Q7=makeQuery(id+"F1.opExtrude","CAP_EDGE",EDGE,{"disambiguationData":[OSD([sQuery(id+"F0.wireOp",EDGE,"E261.left")])],"isStart":true});
            chamfer(context, id + "F5", {"entities" : qUnion([Q0, Q1, Q2, Q3, Q4, Q5, Q6, Q7]), "width" : 0.5 * mm, "tangentPropagation" : true});
        }
    });
